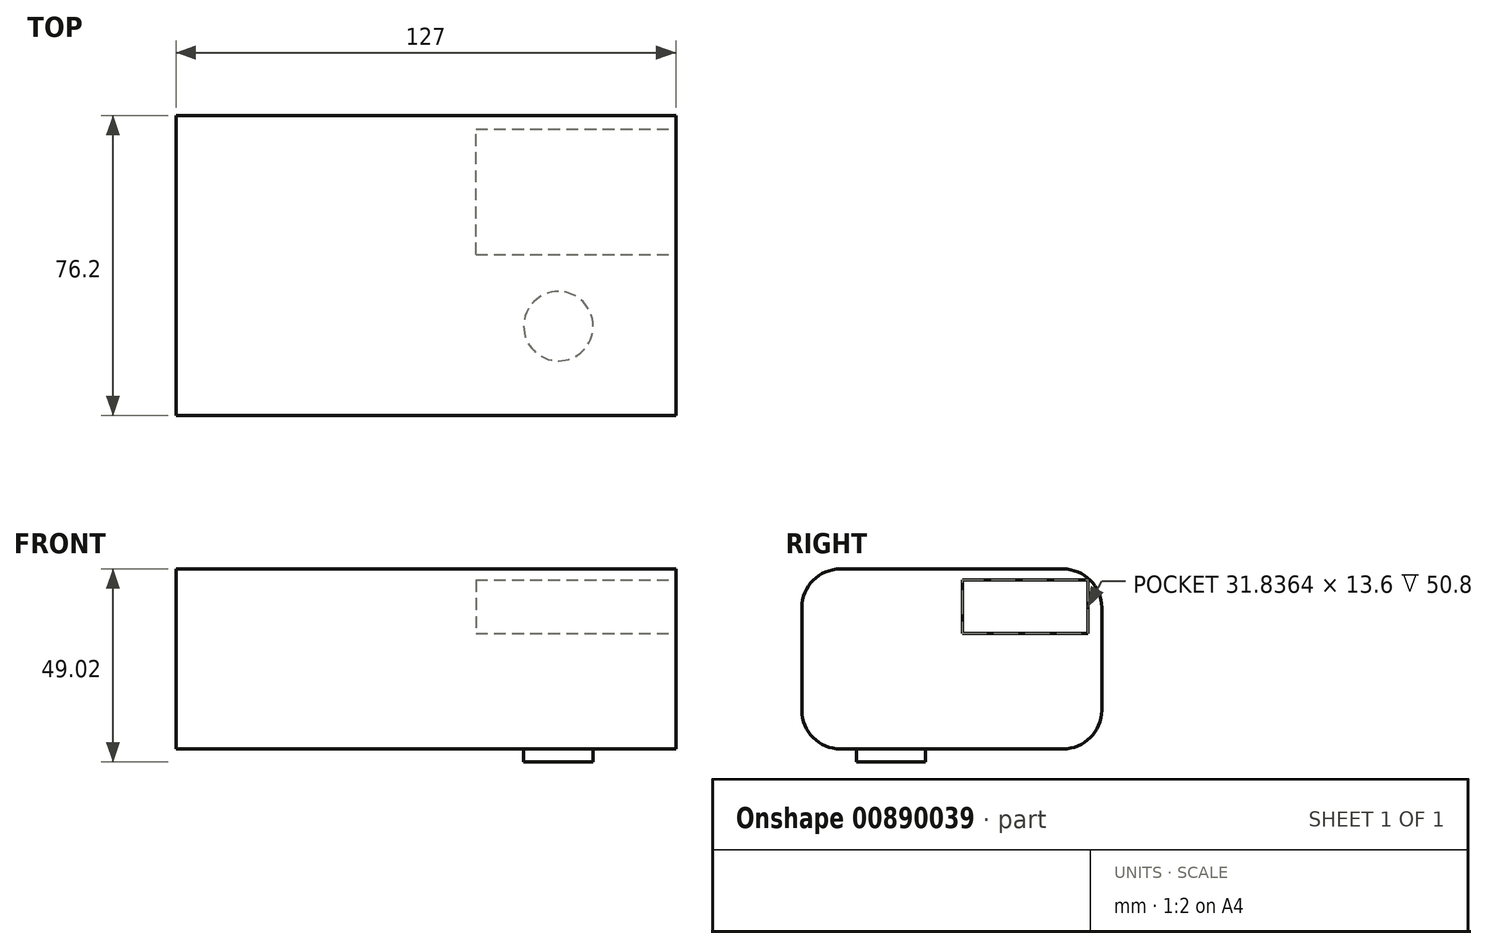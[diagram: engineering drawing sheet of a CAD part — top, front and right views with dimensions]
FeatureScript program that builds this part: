
annotation { "Feature Type Name" : "Feature", "Feature Type Description" : "" }
export const myFeature = defineFeature(function(context is Context, id is Id, definition is map)
    precondition{}
    {
        {
            var Q0;
            Q0=qCreatedBy(makeId("Top.planeOp"),FACE);
            var sketch = newSketch(context, id + "F0", { "sketchPlane" : qUnion([Q0])});
            skLineSegment(sketch, "E0.bottom", {"start": v(63.5, 38.1) * mm, "end": v(-63.5, 38.1) * mm});
            skLineSegment(sketch, "E0.top", {"start": v(63.5, -38.1) * mm, "end": v(-63.5, -38.1) * mm});
            skLineSegment(sketch, "E0.left", {"start": v(63.5, 38.1) * mm, "end": v(63.5, -38.1) * mm});
            skLineSegment(sketch, "E0.right", {"start": v(-63.5, 38.1) * mm, "end": v(-63.5, -38.1) * mm});
            skPoint(sketch, "E0.middle", {"position": v(0, 0) * mm});
            skSolve(sketch);
        }
        {
            var Q0;
            Q0=makeQuery(id+"F0.imprint","IMPRINT",FACE,{"disambiguationData":[TD([[makeQuery(id+"F0.imprint","IMPRINT",EDGE,{"derivedFrom":sQuery(id+"F0.wireOp",EDGE,"E0.bottom")}),1.0]])]});
            extrude(context, id + "F1", {"entities" : qUnion([Q0]), "depth" : 45.72 * mm, "offsetDistance" : 25.4 * mm});
        }
        {
            var Q0;
            Q0=makeQuery(id+"F1.opExtrude","CAP_EDGE",EDGE,{"disambiguationData":[OSD([sQuery(id+"F0.wireOp",EDGE,"E0.top")])],"isStart":false});
            var Q1;
            Q1=makeQuery(id+"F1.opExtrude","CAP_EDGE",EDGE,{"disambiguationData":[OSD([sQuery(id+"F0.wireOp",EDGE,"E0.bottom")])],"isStart":false});
            var Q2;
            Q2=makeQuery(id+"F1.opExtrude","CAP_EDGE",EDGE,{"disambiguationData":[OSD([sQuery(id+"F0.wireOp",EDGE,"E0.top")])],"isStart":true});
            var Q3;
            Q3=makeQuery(id+"F1.opExtrude","CAP_EDGE",EDGE,{"disambiguationData":[OSD([sQuery(id+"F0.wireOp",EDGE,"E0.bottom")])],"isStart":true});
            fillet(context, id + "F2", {"entities" : qUnion([Q0, Q1, Q2, Q3]), "radius" : 9.8 * mm, "tangentPropagation" : true, "allowEdgeOverflow" : false});
        }
        {
            var Q0;
            Q0=makeQuery(id+"F1.opExtrude","CAP_FACE",FACE,{"disambiguationData":[OSD([sQuery(id+"F0.wireOp",EDGE,"E0.bottom"),sQuery(id+"F0.wireOp",EDGE,"E0.top"),sQuery(id+"F0.wireOp",EDGE,"E0.left"),sQuery(id+"F0.wireOp",EDGE,"E0.right")])],"isStart":true});
            var sketch = newSketch(context, id + "F3", { "sketchPlane" : qUnion([Q0])});
            skCircle(sketch, "E1", {"center": v(33.67, 15.42) * mm, "radius": 8.8 * mm});
            skPoint(sketch, "E1.first.point", {"position": v(26.33, 20.3) * mm});
            skPoint(sketch, "E1.second.point", {"position": v(41.88, 12.23) * mm});
            skPoint(sketch, "E1.third.point", {"position": v(30.94, 7.05) * mm});
            skSolve(sketch);
        }
        {
            var Q0;
            Q0 = qSketchRegion(id + "F3", true);
            extrude(context, id + "F4", {"entities" : qUnion([Q0]), "operationType" : NewBodyOperationType.ADD, "depth" : 3.3 * mm, "offsetDistance" : 25.4 * mm});
        }
        {
            var Q0;
            Q0=makeQuery(id+"F1.opExtrude","SWEPT_FACE",FACE,{"disambiguationData":[OSD([sQuery(id+"F0.wireOp",EDGE,"E0.left")])]});
            var sketch = newSketch(context, id + "F5", { "sketchPlane" : qUnion([Q0])});
            skLineSegment(sketch, "E2.bottom", {"start": v(2.79, 42.92) * mm, "end": v(34.63, 42.92) * mm});
            skLineSegment(sketch, "E2.top", {"start": v(2.79, 29.32) * mm, "end": v(34.63, 29.32) * mm});
            skLineSegment(sketch, "E2.left", {"start": v(2.79, 42.92) * mm, "end": v(2.79, 29.32) * mm});
            skLineSegment(sketch, "E2.right", {"start": v(34.63, 42.92) * mm, "end": v(34.63, 29.32) * mm});
            skSolve(sketch);
        }
        {
            var Q0;
            Q0=makeQuery(id+"F5.imprint","IMPRINT",FACE,{"disambiguationData":[TD([[makeQuery(id+"F5.imprint","IMPRINT",EDGE,{"derivedFrom":sQuery(id+"F5.wireOp",EDGE,"E2.bottom")}),-1.0]])]});
            extrude(context, id + "F6", {"entities" : qUnion([Q0]), "operationType" : NewBodyOperationType.REMOVE, "oppositeDirection" : true, "depth" : 50.8 * mm, "offsetDistance" : 25.4 * mm});
        }
    });
